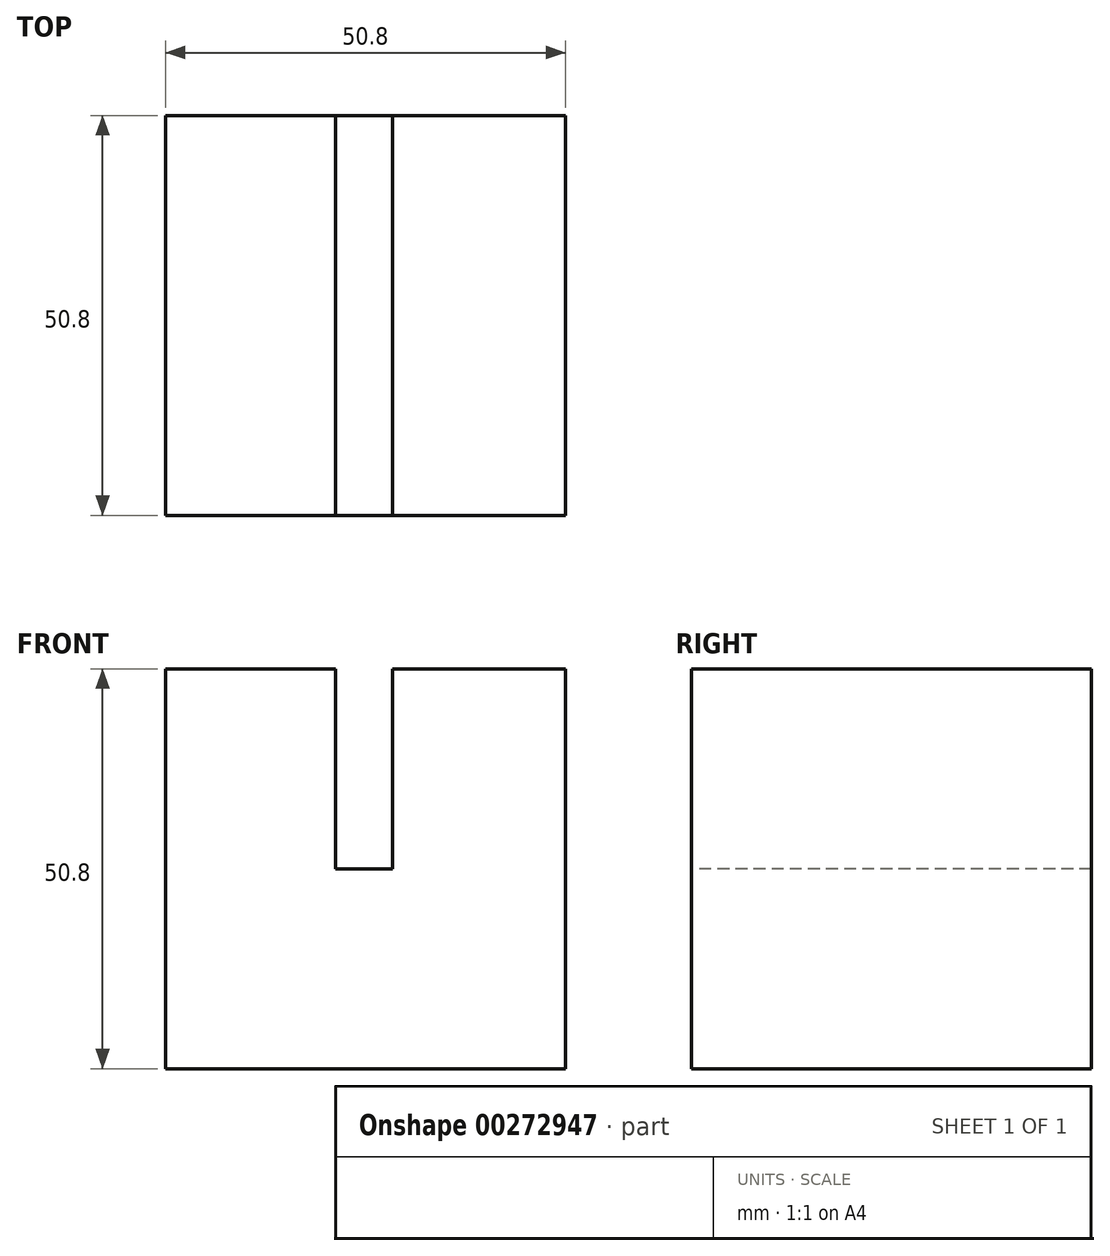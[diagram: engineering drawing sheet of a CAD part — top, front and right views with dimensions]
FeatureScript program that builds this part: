
annotation { "Feature Type Name" : "Feature", "Feature Type Description" : "" }
export const myFeature = defineFeature(function(context is Context, id is Id, definition is map)
    precondition{}
    {
        {
            var Q0;
            Q0=qCreatedBy(makeId("Front.planeOp"),FACE);
            var sketch = newSketch(context, id + "F0", { "sketchPlane" : qUnion([Q0])});
            skLineSegment(sketch, "E0.bottom", {"start": v(0, 0) * mm, "end": v(-50.8, 0) * mm});
            skLineSegment(sketch, "E0.top", {"start": v(0, 50.8) * mm, "end": v(-50.8, 50.8) * mm});
            skLineSegment(sketch, "E0.left", {"start": v(0, 0) * mm, "end": v(0, 50.8) * mm});
            skLineSegment(sketch, "E0.right", {"start": v(-50.8, 0) * mm, "end": v(-50.8, 50.8) * mm});
            skSolve(sketch);
        }
        {
            var Q0;
            Q0 = qSketchRegion(id + "F0", true);
            extrude(context, id + "F1", {"entities" : qUnion([Q0]), "depth" : 50.8 * mm});
        }
        {
            var Q0;
            Q0=makeQuery(id+"F1.opExtrude","SWEPT_FACE",FACE,{"disambiguationData":[OSD([sQuery(id+"F0.wireOp",EDGE,"E0.top")])]});
            var sketch = newSketch(context, id + "F2", { "sketchPlane" : qUnion([Q0])});
            skLineSegment(sketch, "E1.bottom", {"start": v(-21.96, 0) * mm, "end": v(-29.22, 0) * mm});
            skLineSegment(sketch, "E1.top", {"start": v(-21.96, -51.18) * mm, "end": v(-29.22, -51.18) * mm});
            skLineSegment(sketch, "E1.left", {"start": v(-21.96, 0) * mm, "end": v(-21.96, -51.18) * mm});
            skLineSegment(sketch, "E1.right", {"start": v(-29.22, 0) * mm, "end": v(-29.22, -51.18) * mm});
            skPoint(sketch, "E1.middle", {"position": v(-25.59, -25.59) * mm});
            skSolve(sketch);
        }
        {
            var Q0;
            {var subQ0=sQuery(id+"F2.wireOp",EDGE,"E1.bottom");Q0=makeQuery(id+"F2.imprint","IMPRINT",FACE,{"disambiguationData":[TD([[makeQuery(id+"F2.imprint","IMPRINT",EDGE,{"derivedFrom":subQ0}),1.0]])]});}
            extrude(context, id + "F3", {"entities" : qUnion([Q0]), "operationType" : NewBodyOperationType.REMOVE, "oppositeDirection" : true, "depth" : 25.4 * mm});
        }
    });
